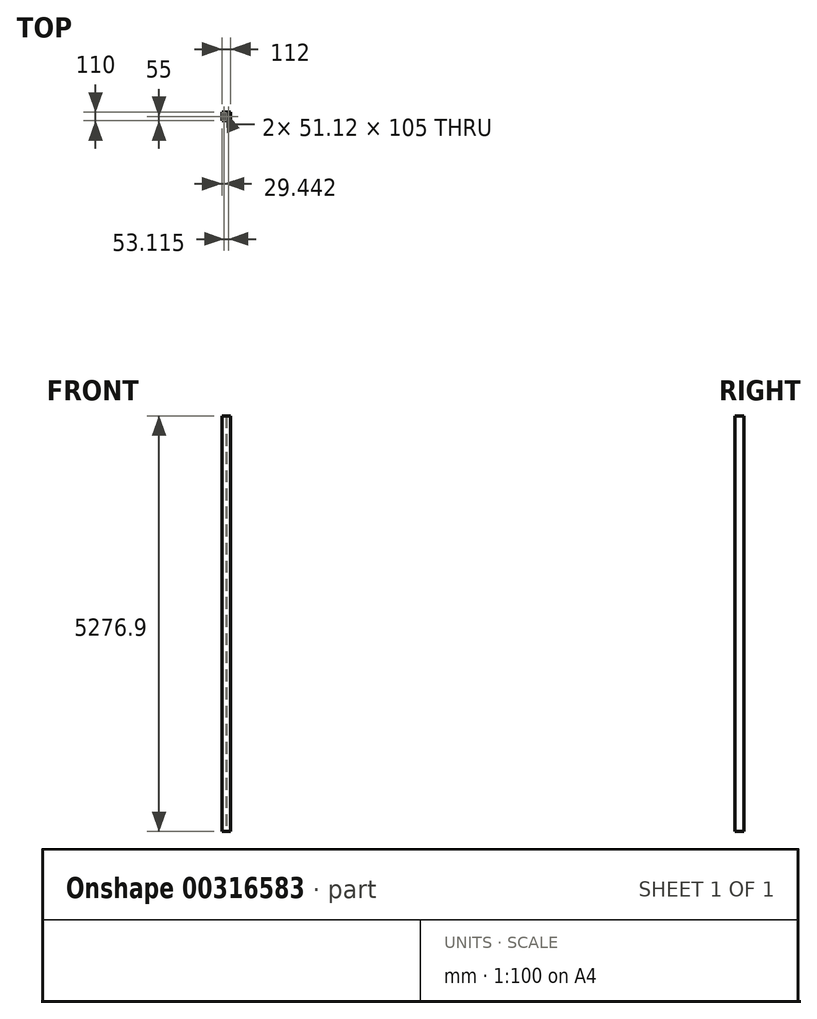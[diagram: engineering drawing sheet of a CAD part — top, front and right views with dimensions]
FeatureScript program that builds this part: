
annotation { "Feature Type Name" : "Feature", "Feature Type Description" : "" }
export const myFeature = defineFeature(function(context is Context, id is Id, definition is map)
    precondition{}
    {
        {
            var Q0;
            Q0=qCreatedBy(makeId("Top.planeOp"),FACE);
            var sketch = newSketch(context, id + "F0", { "sketchPlane" : qUnion([Q0])});
            skLineSegment(sketch, "E0.bottom", {"start": v(-56, 55) * mm, "end": v(56, 55) * mm});
            skLineSegment(sketch, "E0.top", {"start": v(-56, -55) * mm, "end": v(56, -55) * mm});
            skLineSegment(sketch, "E0.left", {"start": v(-56, 55) * mm, "end": v(-56, -55) * mm});
            skLineSegment(sketch, "E0.right", {"start": v(56, 55) * mm, "end": v(56, -55) * mm});
            skPoint(sketch, "E0.middle", {"position": v(0, 0) * mm});
            skLineSegment(sketch, "E1.bottom", {"start": v(-52.12, 52.5) * mm, "end": v(52.12, 52.5) * mm});
            skLineSegment(sketch, "E1.top", {"start": v(-52.12, -52.5) * mm, "end": v(52.12, -52.5) * mm});
            skLineSegment(sketch, "E1.left", {"start": v(-52.12, 52.5) * mm, "end": v(-52.12, -52.5) * mm});
            skLineSegment(sketch, "E1.right", {"start": v(52.12, 52.5) * mm, "end": v(52.12, -52.5) * mm});
            skLineSegment(sketch, "E2", {"start": v(0, -52.5) * mm, "end": v(1, -52.5) * mm});
            skLineSegment(sketch, "E3", {"start": v(1, -52.5) * mm, "end": v(1, 52.5) * mm});
            skLineSegment(sketch, "E4", {"start": v(1, 52.5) * mm, "end": v(-1, 52.5) * mm});
            skLineSegment(sketch, "E5", {"start": v(-1, 52.5) * mm, "end": v(-1, -52.5) * mm});
            skLineSegment(sketch, "E6", {"start": v(-1, -52.5) * mm, "end": v(1, -52.5) * mm});
            skSolve(sketch);
        }
        {
            var Q0;
            {var subQ4=sQuery(id+"F0.wireOp",EDGE,"E3");Q0=makeQuery(id+"F0.imprint","IMPRINT",FACE,{"disambiguationData":[TD([[makeQuery(id+"F0.imprint","IMPRINT",EDGE,{"derivedFrom":subQ4}),1.0]])]});}
            var Q1;
            Q1=makeQuery(id+"F0.imprint","IMPRINT",FACE,{"disambiguationData":[TD([[makeQuery(id+"F0.imprint","IMPRINT",EDGE,{"derivedFrom":sQuery(id+"F0.wireOp",EDGE,"E0.bottom")}),-1.0]])]});
            extrude(context, id + "F1", {"entities" : qUnion([Q0, Q1]), "depth" : 5276.9 * mm});
        }
    });
